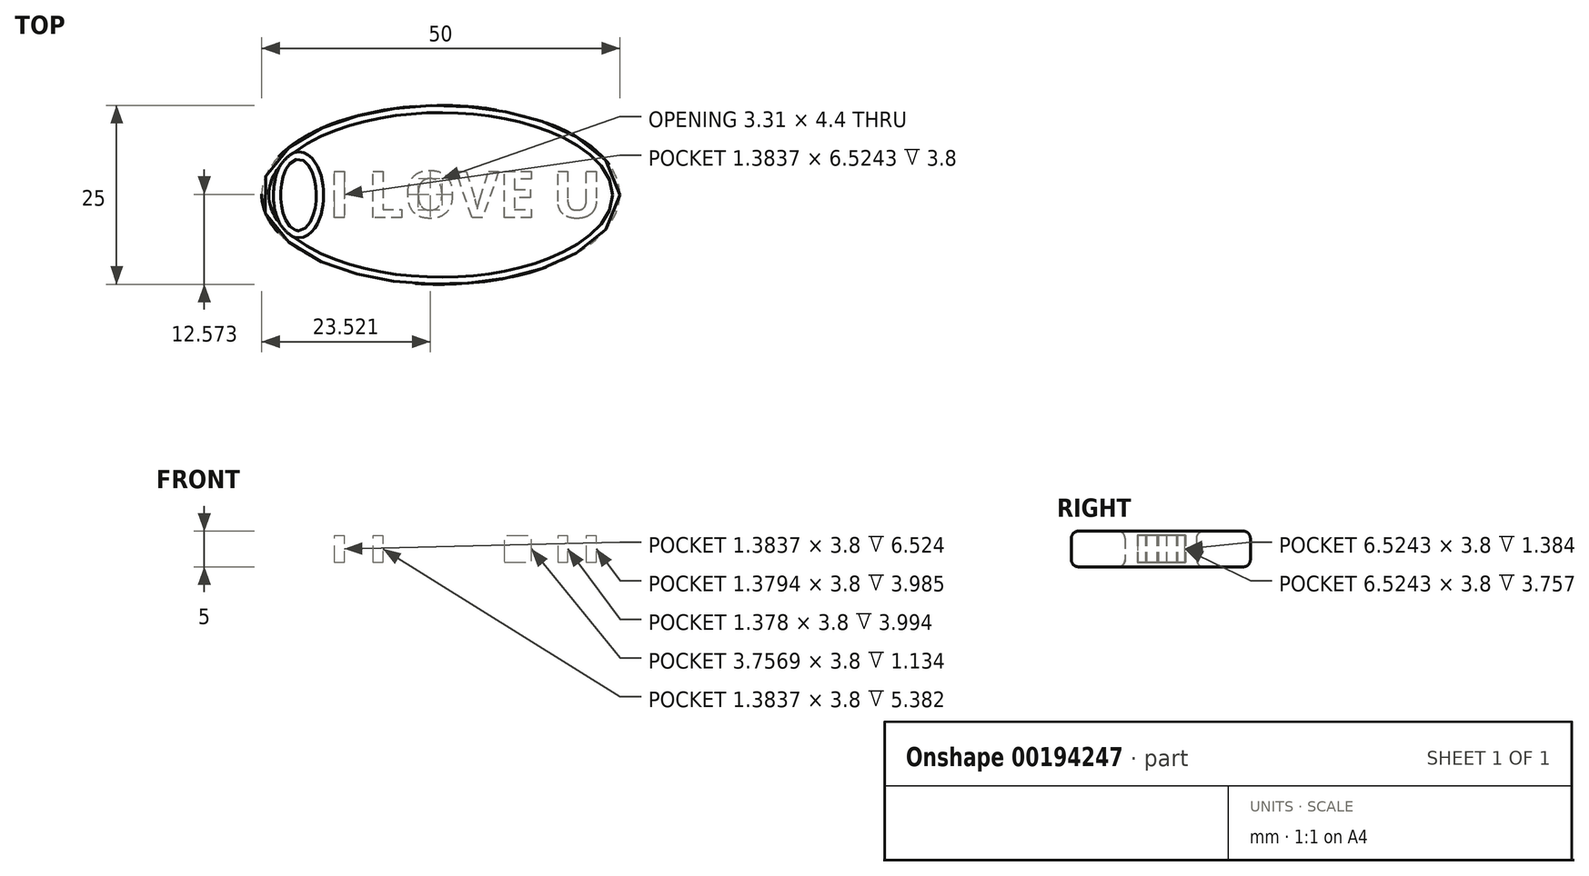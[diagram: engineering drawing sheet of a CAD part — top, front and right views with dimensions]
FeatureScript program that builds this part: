
annotation { "Feature Type Name" : "Feature", "Feature Type Description" : "" }
export const myFeature = defineFeature(function(context is Context, id is Id, definition is map)
    precondition{}
    {
        {
            var Q0;
            Q0=qCreatedBy(makeId("Top.planeOp"),FACE);
            var sketch = newSketch(context, id + "F0", { "sketchPlane" : qUnion([Q0])});
            skEllipse(sketch, "E0", {"center": v(0, 0) * mm, "majorRadius": 25 * mm, "minorRadius": 12.5 * mm, "majorAxis": v(1, 0)});
            skEllipse(sketch, "E1", {"center": v(-19.86, 0) * mm, "majorRadius": 5 * mm, "minorRadius": 2.5 * mm, "majorAxis": v(0, -1)});
            skSolve(sketch);
        }
        {
            var Q0;
            Q0 = qSketchRegion(id + "F0", true);
            extrude(context, id + "F1", {"entities" : qUnion([Q0]), "depth" : 5 * mm, "symmetric" : true});
        }
        {
            var Q0;
            Q0=makeQuery(id+"F1.opExtrude","CAP_EDGE",EDGE,{"disambiguationData":[OSD([sQuery(id+"F0.wireOp",EDGE,"E1")])],"isStart":false});
            var Q1;
            Q1=makeQuery(id+"F1.opExtrude","CAP_EDGE",EDGE,{"disambiguationData":[OSD([sQuery(id+"F0.wireOp",EDGE,"E0")])],"isStart":false});
            var Q2;
            Q2=makeQuery(id+"F1.opExtrude","CAP_EDGE",EDGE,{"disambiguationData":[OSD([sQuery(id+"F0.wireOp",EDGE,"E0")])],"isStart":true});
            var Q3;
            Q3=makeQuery(id+"F1.opExtrude","CAP_EDGE",EDGE,{"disambiguationData":[OSD([sQuery(id+"F0.wireOp",EDGE,"E1")])],"isStart":true});
            fillet(context, id + "F2", {"entities" : qUnion([Q0, Q1, Q2, Q3]), "radius" : 1 * mm, "tangentPropagation" : true, "allowEdgeOverflow" : false});
        }
        {
            var Q0;
            Q0=qCreatedBy(makeId("Top.planeOp"),FACE);
            var sketch = newSketch(context, id + "F3", { "sketchPlane" : qUnion([Q0])});
            skText(sketch, "E2", { "text": "I LOVE U", "fontName": "OpenSans-Bold.ttf"});
            const initialGuessF3  = {"E2": [-0.01568, -0.0032, 1, 0, 0.00658]};
            skSetInitialGuess(sketch, initialGuessF3);
            skSolve(sketch);
        }
        {
            var Q0;
            Q0 = qSketchRegion(id + "F3", true);
            extrude(context, id + "F4", {"entities" : qUnion([Q0]), "operationType" : NewBodyOperationType.REMOVE, "depth" : 3.8 * mm, "symmetric" : true});
        }
    });
